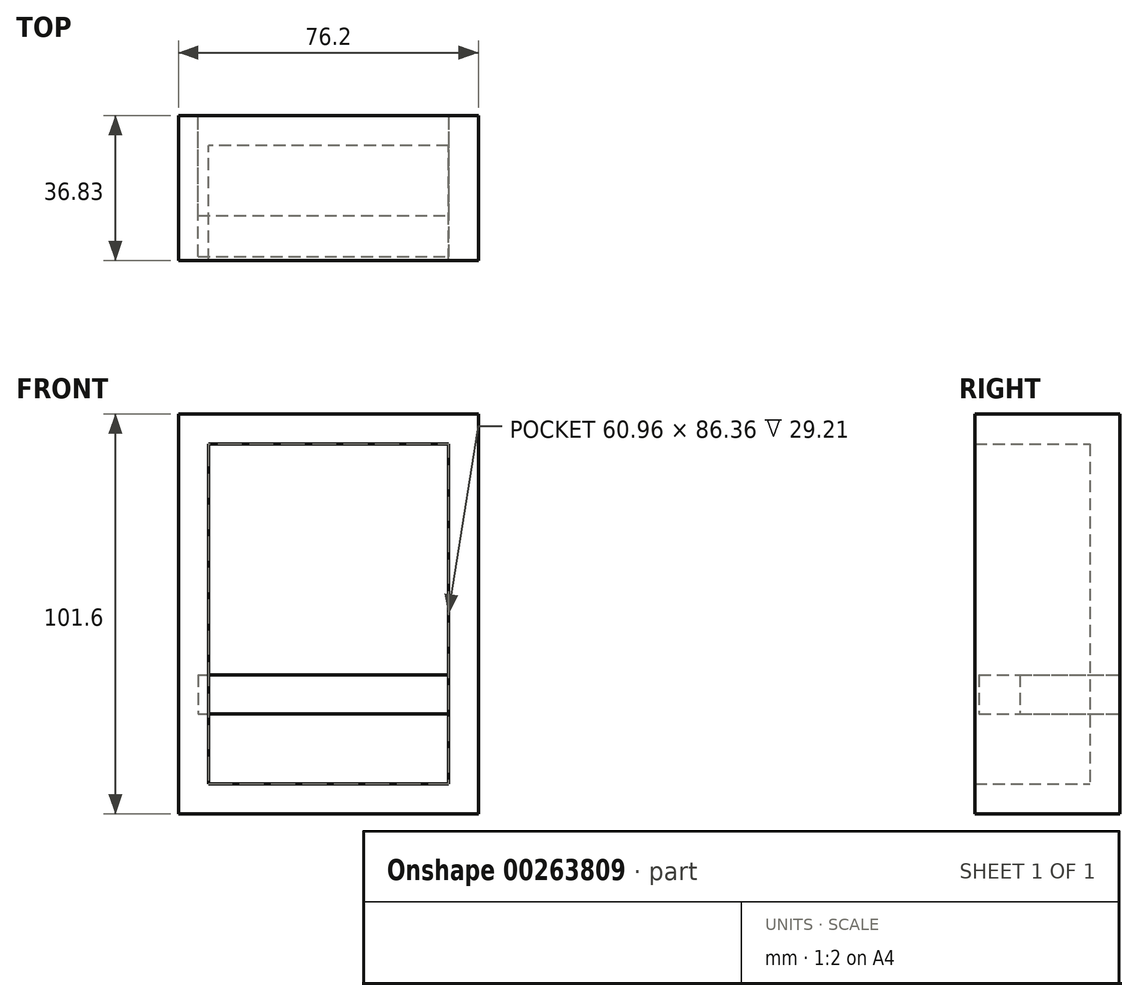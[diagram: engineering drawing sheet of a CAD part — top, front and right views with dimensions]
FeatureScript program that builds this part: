
annotation { "Feature Type Name" : "Feature", "Feature Type Description" : "" }
export const myFeature = defineFeature(function(context is Context, id is Id, definition is map)
    precondition{}
    {
        {
            var Q0;
            Q0=qCreatedBy(makeId("Front.planeOp"),FACE);
            var sketch = newSketch(context, id + "F0", { "sketchPlane" : qUnion([Q0])});
            skLineSegment(sketch, "E0.bottom", {"start": v(38.1, 50.8) * mm, "end": v(-38.1, 50.8) * mm});
            skLineSegment(sketch, "E0.top", {"start": v(38.1, -50.8) * mm, "end": v(-38.1, -50.8) * mm});
            skLineSegment(sketch, "E0.left", {"start": v(38.1, 50.8) * mm, "end": v(38.1, -50.8) * mm});
            skLineSegment(sketch, "E0.right", {"start": v(-38.1, 50.8) * mm, "end": v(-38.1, -50.8) * mm});
            skPoint(sketch, "E0.middle", {"position": v(0, 0) * mm});
            skSolve(sketch);
        }
        {
            var Q0;
            Q0 = qSketchRegion(id + "F0", true);
            extrude(context, id + "F1", {"entities" : qUnion([Q0]), "depth" : 36.83 * mm});
        }
        {
            var Q0;
            Q0=makeQuery(id+"F1.opExtrude","CAP_FACE",FACE,{"disambiguationData":[OSD([sQuery(id+"F0.wireOp",EDGE,"E0.bottom"),sQuery(id+"F0.wireOp",EDGE,"E0.top"),sQuery(id+"F0.wireOp",EDGE,"E0.left"),sQuery(id+"F0.wireOp",EDGE,"E0.right")])],"isStart":false});
            shell(context, id + "F2", {"entities" : qUnion([Q0]), "thickness" : 7.62 * mm});
        }
        {
            var Q0;
            Q0=qCreatedBy(makeId("Front.planeOp"),FACE);
            var sketch = newSketch(context, id + "F3", { "sketchPlane" : qUnion([Q0])});
            skLineSegment(sketch, "E1", {"start": v(-30.6, -15.49) * mm, "end": v(31.16, -15.49) * mm});
            skLineSegment(sketch, "E2.bottom", {"start": v(-33.09, -15.49) * mm, "end": v(30.69, -15.49) * mm});
            skLineSegment(sketch, "E2.top", {"start": v(-33.09, -25.44) * mm, "end": v(30.69, -25.44) * mm});
            skLineSegment(sketch, "E2.left", {"start": v(-33.09, -15.49) * mm, "end": v(-33.09, -25.44) * mm});
            skLineSegment(sketch, "E2.right", {"start": v(30.69, -15.49) * mm, "end": v(30.69, -25.44) * mm});
            skSolve(sketch);
        }
        {
            var Q0;
            Q0 = qSketchRegion(id + "F3", true);
            extrude(context, id + "F4", {"entities" : qUnion([Q0]), "depth" : 25.4 * mm});
        }
        {
            var Q0;
            Q0 = qSketchRegion(id + "F3", true);
            extrude(context, id + "F5", {"entities" : qUnion([Q0]), "depth" : 35.81 * mm});
        }
    });
